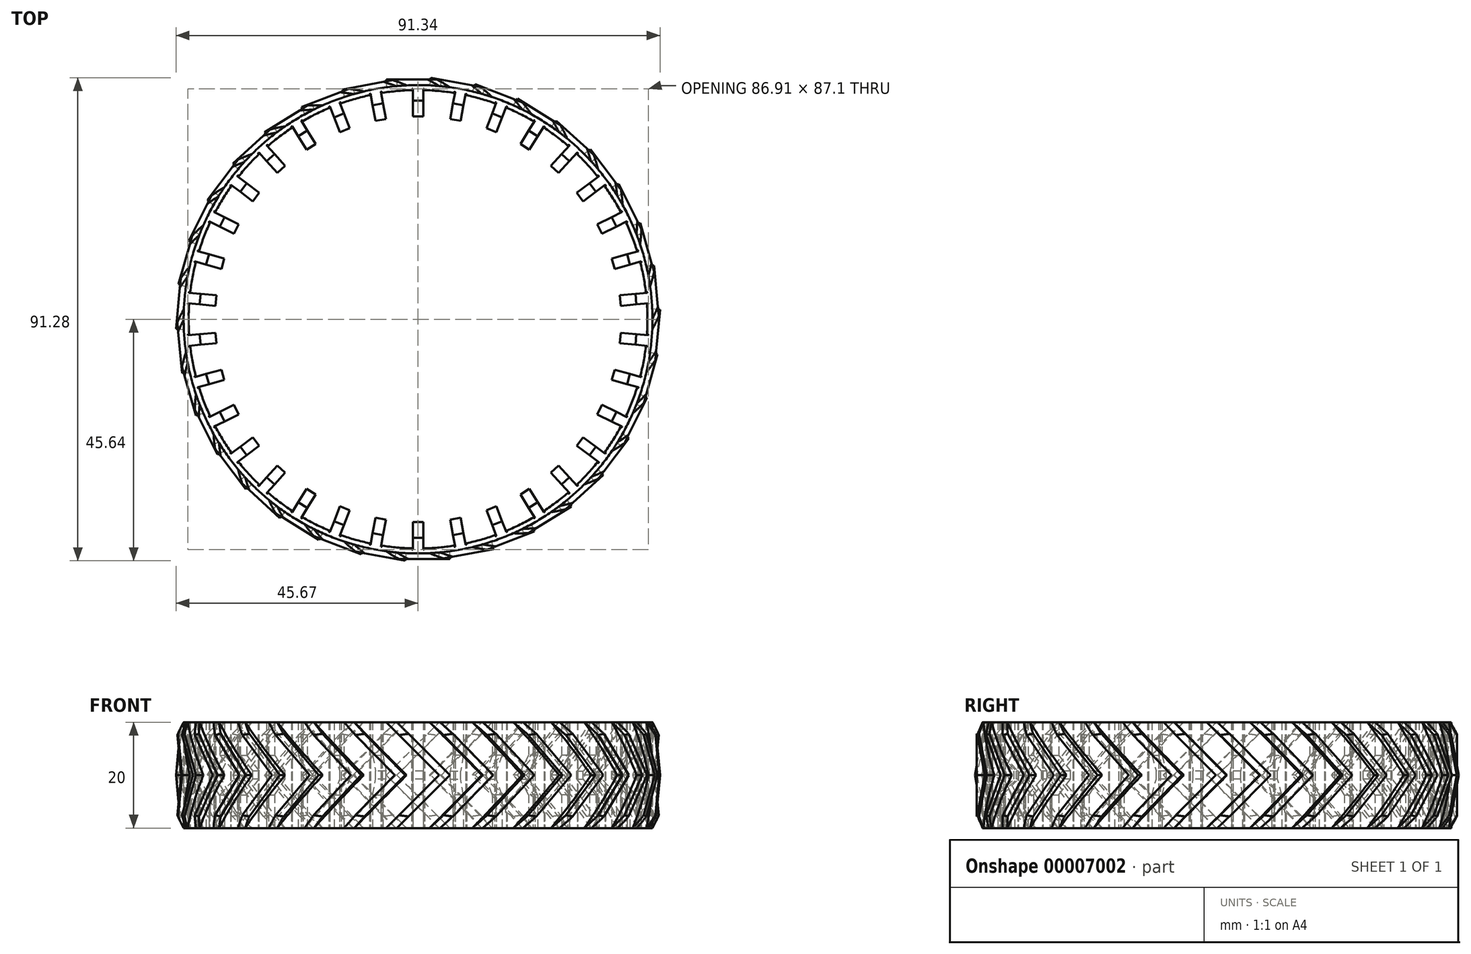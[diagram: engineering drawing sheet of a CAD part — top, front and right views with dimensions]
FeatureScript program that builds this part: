
annotation { "Feature Type Name" : "Feature", "Feature Type Description" : "" }
export const myFeature = defineFeature(function(context is Context, id is Id, definition is map)
    precondition{}
    {
        {
            var Q0;
            Q0=qCreatedBy(makeId("Front.planeOp"),FACE);
            cPlane(context, id + "F0", {"entities" : qUnion([Q0]), "cplaneType" : CPlaneType.OFFSET, "offset" : 86.62 * mm / 2, "width" : 150 * mm, "height" : 150 * mm});
        }
        {
            var Q0;
            Q0=qCreatedBy(id+"F0.planeOp",FACE);
            var sketch = newSketch(context, id + "F1", { "sketchPlane" : qUnion([Q0])});
            skLineSegment(sketch, "E0", {"start": v(-5, -10) * mm, "end": v(-6, -10) * mm});
            skLineSegment(sketch, "E1", {"start": v(-5, -10) * mm, "end": v(-4, -10) * mm});
            skLineSegment(sketch, "E2", {"start": v(-5, 10) * mm, "end": v(-4, 10) * mm});
            skLineSegment(sketch, "E3", {"start": v(-5, 10) * mm, "end": v(-6, 10) * mm});
            skLineSegment(sketch, "E4", {"start": v(-6, 10) * mm, "end": v(4, 0) * mm});
            skLineSegment(sketch, "E5", {"start": v(4, 0) * mm, "end": v(-6, -10) * mm});
            skLineSegment(sketch, "E6", {"start": v(-4, -10) * mm, "end": v(6, 0) * mm});
            skLineSegment(sketch, "E7", {"start": v(6, 0) * mm, "end": v(-4, 10) * mm});
            skSolve(sketch);
        }
        {
            var Q0;
            Q0 = qSketchRegion(id + "F1", true);
            extrude(context, id + "F2", {"entities" : qUnion([Q0]), "depth" : 2 * mm, "hasSecondDirection" : true, "secondDirectionOppositeDirection" : true, "secondDirectionDepth" : 2 * mm});
        }
        {
            var Q0;
            Q0=qCreatedBy(makeId("Front.planeOp"),FACE);
            var sketch = newSketch(context, id + "F3", { "sketchPlane" : qUnion([Q0])});
            skLineSegment(sketch, "E8", {"start": v(0, 0) * mm, "end": v(0, 18.84) * mm, "construction": true});
            skSolve(sketch);
        }
        {
            var Q0;
            Q0=makeQuery(id+"F2.opExtrude","SWEPT_BODY",BODY,{"disambiguationData":[OSD([sQuery(id+"F1.wireOp",EDGE,"E0"),sQuery(id+"F1.wireOp",EDGE,"E1"),sQuery(id+"F1.wireOp",EDGE,"E2"),sQuery(id+"F1.wireOp",EDGE,"E3"),sQuery(id+"F1.wireOp",EDGE,"E4"),sQuery(id+"F1.wireOp",EDGE,"E5"),sQuery(id+"F1.wireOp",EDGE,"E6"),sQuery(id+"F1.wireOp",EDGE,"E7")])]});
            var Q1;
            Q1=sQuery(id+"F3.wireOp",EDGE,"E8");
            circularPattern(context, id + "F4", {"operationType" : NewBodyOperationType.ADD, "entities" : qUnion([Q0]), "axis" : qUnion([Q1]), "angle" : 360 * degree, "instanceCount" : 34, "equalSpace" : true});
        }
        {
            var Q0;
            Q0=qCreatedBy(makeId("Top.planeOp"),FACE);
            var sketch = newSketch(context, id + "F5", { "sketchPlane" : qUnion([Q0])});
            skCircle(sketch, "E9", {"center": v(0, 0) * mm, "radius": 43.31 * mm});
            skSolve(sketch);
        }
        {
            var Q0;
            Q0 = qSketchRegion(id + "F5", true);
            extrude(context, id + "F6", {"entities" : qUnion([Q0]), "operationType" : NewBodyOperationType.REMOVE, "oppositeDirection" : true, "depth" : 25 * mm, "hasSecondDirection" : true, "secondDirectionOppositeDirection" : false, "secondDirectionDepth" : 25 * mm});
        }
        {
            var Q0;
            Q0=qCreatedBy(makeId("Top.planeOp"),FACE);
            var sketch = newSketch(context, id + "F7", { "sketchPlane" : qUnion([Q0])});
            skLineSegment(sketch, "E10", {"start": v(0, 41.31) * mm, "end": v(1, 41.31) * mm});
            skLineSegment(sketch, "E11", {"start": v(0, 41.31) * mm, "end": v(-1, 41.31) * mm});
            skLineSegment(sketch, "E12", {"start": v(1, 41.31) * mm, "end": v(1, 43.3) * mm});
            skLineSegment(sketch, "E13", {"start": v(-1, 41.31) * mm, "end": v(-1, 43.3) * mm});
            skArc(sketch, "E14", {"start": v(1.25, 43.3) * mm, "mid": v(1.18, 43.47) * mm, "end": v(1, 43.55) * mm});
            skLineSegment(sketch, "E15", {"start": v(-1, 43.3) * mm, "end": v(-1, 43.55) * mm});
            skLineSegment(sketch, "E16", {"start": v(1, 43.3) * mm, "end": v(1, 43.55) * mm});
            skLineSegment(sketch, "E17", {"start": v(1.25, 43.3) * mm, "end": v(1.25, 43.3) * mm});
            skLineSegment(sketch, "E18", {"start": v(-1.25, 43.3) * mm, "end": v(-1.25, 43.3) * mm});
            skArc(sketch, "E19.trimOffspring", {"start": v(-1, 43.55) * mm, "mid": v(-1.18, 43.47) * mm, "end": v(-1.25, 43.3) * mm});
            skArc(sketch, "E20.trimOffspring", {"start": v(6.73, 42.78) * mm, "mid": v(4, 43.13) * mm, "end": v(1.25, 43.3) * mm});
            skArc(sketch, "E21.1.0", {"start": v(-1.25, 43.3) * mm, "mid": v(-4, 43.13) * mm, "end": v(-6.73, 42.78) * mm});
            skLineSegment(sketch, "E21.1.1", {"start": v(-6.6, 40.8) * mm, "end": v(-6.97, 42.74) * mm});
            skLineSegment(sketch, "E21.1.2", {"start": v(-8.57, 40.42) * mm, "end": v(-8.94, 42.38) * mm});
            skLineSegment(sketch, "E21.1.3", {"start": v(-7.6, 40.6) * mm, "end": v(-6.6, 40.8) * mm});
            skLineSegment(sketch, "E21.1.4", {"start": v(-7.6, 40.6) * mm, "end": v(-8.57, 40.42) * mm});
            skLineSegment(sketch, "E21.1.5", {"start": v(-8.94, 42.38) * mm, "end": v(-8.98, 42.62) * mm});
            skArc(sketch, "E21.1.6", {"start": v(-8.98, 42.62) * mm, "mid": v(-9.15, 42.52) * mm, "end": v(-9.18, 42.33) * mm});
            skArc(sketch, "E21.1.7", {"start": v(-6.73, 42.78) * mm, "mid": v(-6.83, 42.95) * mm, "end": v(-7.02, 43) * mm});
            skLineSegment(sketch, "E21.1.8", {"start": v(-6.97, 42.74) * mm, "end": v(-7.02, 43) * mm});
            skLineSegment(sketch, "E21.1.9", {"start": v(-6.73, 42.79) * mm, "end": v(-6.73, 42.78) * mm});
            skLineSegment(sketch, "E21.1.10", {"start": v(-9.18, 42.33) * mm, "end": v(-9.18, 42.33) * mm});
            skArc(sketch, "E21.2.0", {"start": v(-9.18, 42.33) * mm, "mid": v(-11.85, 41.66) * mm, "end": v(-14.47, 40.82) * mm});
            skLineSegment(sketch, "E21.2.1", {"start": v(-14, 38.88) * mm, "end": v(-14.7, 40.74) * mm});
            skLineSegment(sketch, "E21.2.2", {"start": v(-15.86, 38.16) * mm, "end": v(-16.57, 40.01) * mm});
            skLineSegment(sketch, "E21.2.3", {"start": v(-14.92, 38.52) * mm, "end": v(-14, 38.88) * mm});
            skLineSegment(sketch, "E21.2.4", {"start": v(-14.92, 38.52) * mm, "end": v(-15.86, 38.16) * mm});
            skLineSegment(sketch, "E21.2.5", {"start": v(-16.57, 40.01) * mm, "end": v(-16.66, 40.25) * mm});
            skArc(sketch, "E21.2.6", {"start": v(-16.66, 40.25) * mm, "mid": v(-16.8, 40.11) * mm, "end": v(-16.8, 39.92) * mm});
            skArc(sketch, "E21.2.7", {"start": v(-14.47, 40.82) * mm, "mid": v(-14.6, 40.96) * mm, "end": v(-14.8, 40.97) * mm});
            skLineSegment(sketch, "E21.2.8", {"start": v(-14.7, 40.74) * mm, "end": v(-14.8, 40.97) * mm});
            skLineSegment(sketch, "E21.2.9", {"start": v(-14.47, 40.82) * mm, "end": v(-14.47, 40.82) * mm});
            skLineSegment(sketch, "E21.2.10", {"start": v(-16.8, 39.92) * mm, "end": v(-16.8, 39.92) * mm});
            skArc(sketch, "E21.3.0", {"start": v(-16.8, 39.92) * mm, "mid": v(-19.3, 38.77) * mm, "end": v(-21.73, 37.47) * mm});
            skLineSegment(sketch, "E21.3.1", {"start": v(-20.9, 35.65) * mm, "end": v(-21.94, 37.34) * mm});
            skLineSegment(sketch, "E21.3.2", {"start": v(-22.6, 34.6) * mm, "end": v(-23.64, 36.29) * mm});
            skLineSegment(sketch, "E21.3.3", {"start": v(-21.75, 35.12) * mm, "end": v(-20.9, 35.65) * mm});
            skLineSegment(sketch, "E21.3.4", {"start": v(-21.75, 35.12) * mm, "end": v(-22.6, 34.6) * mm});
            skLineSegment(sketch, "E21.3.5", {"start": v(-23.64, 36.29) * mm, "end": v(-23.78, 36.5) * mm});
            skArc(sketch, "E21.3.6", {"start": v(-23.78, 36.5) * mm, "mid": v(-23.89, 36.34) * mm, "end": v(-23.85, 36.15) * mm});
            skArc(sketch, "E21.3.7", {"start": v(-21.73, 37.47) * mm, "mid": v(-21.88, 37.58) * mm, "end": v(-22.08, 37.55) * mm});
            skLineSegment(sketch, "E21.3.8", {"start": v(-21.94, 37.34) * mm, "end": v(-22.08, 37.55) * mm});
            skLineSegment(sketch, "E21.3.9", {"start": v(-21.73, 37.47) * mm, "end": v(-21.73, 37.47) * mm});
            skLineSegment(sketch, "E21.3.10", {"start": v(-23.86, 36.16) * mm, "end": v(-23.85, 36.15) * mm});
            skArc(sketch, "E21.4.0", {"start": v(-23.85, 36.15) * mm, "mid": v(-26.1, 34.56) * mm, "end": v(-28.24, 32.84) * mm});
            skLineSegment(sketch, "E21.4.1", {"start": v(-27.1, 31.2) * mm, "end": v(-28.43, 32.67) * mm});
            skLineSegment(sketch, "E21.4.2", {"start": v(-28.57, 29.85) * mm, "end": v(-29.9, 31.32) * mm});
            skLineSegment(sketch, "E21.4.3", {"start": v(-27.83, 30.53) * mm, "end": v(-27.1, 31.2) * mm});
            skLineSegment(sketch, "E21.4.4", {"start": v(-27.83, 30.53) * mm, "end": v(-28.57, 29.85) * mm});
            skLineSegment(sketch, "E21.4.5", {"start": v(-29.9, 31.32) * mm, "end": v(-30.08, 31.5) * mm});
            skArc(sketch, "E21.4.6", {"start": v(-30.08, 31.5) * mm, "mid": v(-30.16, 31.33) * mm, "end": v(-30.09, 31.15) * mm});
            skArc(sketch, "E21.4.7", {"start": v(-28.24, 32.84) * mm, "mid": v(-28.42, 32.92) * mm, "end": v(-28.6, 32.86) * mm});
            skLineSegment(sketch, "E21.4.8", {"start": v(-28.43, 32.67) * mm, "end": v(-28.6, 32.86) * mm});
            skLineSegment(sketch, "E21.4.9", {"start": v(-28.24, 32.84) * mm, "end": v(-28.24, 32.84) * mm});
            skLineSegment(sketch, "E21.4.10", {"start": v(-30.1, 31.16) * mm, "end": v(-30.09, 31.15) * mm});
            skArc(sketch, "E21.5.0", {"start": v(-30.09, 31.15) * mm, "mid": v(-32, 29.18) * mm, "end": v(-33.8, 27.09) * mm});
            skLineSegment(sketch, "E21.5.1", {"start": v(-32.36, 25.7) * mm, "end": v(-33.95, 26.9) * mm});
            skLineSegment(sketch, "E21.5.2", {"start": v(-33.57, 24.1) * mm, "end": v(-35.16, 25.3) * mm});
            skLineSegment(sketch, "E21.5.3", {"start": v(-32.97, 24.9) * mm, "end": v(-32.36, 25.7) * mm});
            skLineSegment(sketch, "E21.5.4", {"start": v(-32.97, 24.9) * mm, "end": v(-33.57, 24.1) * mm});
            skLineSegment(sketch, "E21.5.5", {"start": v(-35.16, 25.3) * mm, "end": v(-35.36, 25.45) * mm});
            skArc(sketch, "E21.5.6", {"start": v(-35.36, 25.45) * mm, "mid": v(-35.4, 25.26) * mm, "end": v(-35.3, 25.1) * mm});
            skArc(sketch, "E21.5.7", {"start": v(-33.8, 27.09) * mm, "mid": v(-33.98, 27.14) * mm, "end": v(-34.15, 27.04) * mm});
            skLineSegment(sketch, "E21.5.8", {"start": v(-33.95, 26.9) * mm, "end": v(-34.15, 27.04) * mm});
            skLineSegment(sketch, "E21.5.9", {"start": v(-33.8, 27.09) * mm, "end": v(-33.8, 27.09) * mm});
            skLineSegment(sketch, "E21.5.10", {"start": v(-35.3, 25.1) * mm, "end": v(-35.3, 25.1) * mm});
            skArc(sketch, "E21.6.0", {"start": v(-35.3, 25.1) * mm, "mid": v(-36.82, 22.8) * mm, "end": v(-38.2, 20.42) * mm});
            skLineSegment(sketch, "E21.6.1", {"start": v(-36.53, 19.3) * mm, "end": v(-38.31, 20.2) * mm});
            skLineSegment(sketch, "E21.6.2", {"start": v(-37.42, 17.52) * mm, "end": v(-39.2, 18.4) * mm});
            skLineSegment(sketch, "E21.6.3", {"start": v(-36.98, 18.41) * mm, "end": v(-36.53, 19.3) * mm});
            skLineSegment(sketch, "E21.6.4", {"start": v(-36.98, 18.41) * mm, "end": v(-37.42, 17.52) * mm});
            skLineSegment(sketch, "E21.6.5", {"start": v(-39.2, 18.4) * mm, "end": v(-39.43, 18.52) * mm});
            skArc(sketch, "E21.6.6", {"start": v(-39.43, 18.52) * mm, "mid": v(-39.44, 18.32) * mm, "end": v(-39.31, 18.18) * mm});
            skArc(sketch, "E21.6.7", {"start": v(-38.2, 20.42) * mm, "mid": v(-38.39, 20.43) * mm, "end": v(-38.54, 20.3) * mm});
            skLineSegment(sketch, "E21.6.8", {"start": v(-38.31, 20.2) * mm, "end": v(-38.54, 20.3) * mm});
            skLineSegment(sketch, "E21.6.9", {"start": v(-38.2, 20.42) * mm, "end": v(-38.2, 20.42) * mm});
            skLineSegment(sketch, "E21.6.10", {"start": v(-39.32, 18.18) * mm, "end": v(-39.31, 18.18) * mm});
            skArc(sketch, "E21.7.0", {"start": v(-39.31, 18.18) * mm, "mid": v(-40.39, 15.65) * mm, "end": v(-41.3, 13.05) * mm});
            skLineSegment(sketch, "E21.7.1", {"start": v(-39.46, 12.27) * mm, "end": v(-41.37, 12.81) * mm});
            skLineSegment(sketch, "E21.7.2", {"start": v(-40, 10.34) * mm, "end": v(-41.92, 10.89) * mm});
            skLineSegment(sketch, "E21.7.3", {"start": v(-39.73, 11.3) * mm, "end": v(-39.46, 12.27) * mm});
            skLineSegment(sketch, "E21.7.4", {"start": v(-39.73, 11.3) * mm, "end": v(-40, 10.34) * mm});
            skLineSegment(sketch, "E21.7.5", {"start": v(-41.92, 10.89) * mm, "end": v(-42.16, 10.96) * mm});
            skArc(sketch, "E21.7.6", {"start": v(-42.16, 10.96) * mm, "mid": v(-42.14, 10.76) * mm, "end": v(-41.98, 10.65) * mm});
            skArc(sketch, "E21.7.7", {"start": v(-41.3, 13.05) * mm, "mid": v(-41.5, 13.03) * mm, "end": v(-41.61, 12.88) * mm});
            skLineSegment(sketch, "E21.7.8", {"start": v(-41.37, 12.81) * mm, "end": v(-41.61, 12.88) * mm});
            skLineSegment(sketch, "E21.7.9", {"start": v(-41.3, 13.05) * mm, "end": v(-41.3, 13.05) * mm});
            skLineSegment(sketch, "E21.7.10", {"start": v(-41.99, 10.65) * mm, "end": v(-41.98, 10.65) * mm});
            skArc(sketch, "E21.8.0", {"start": v(-41.98, 10.65) * mm, "mid": v(-42.57, 7.96) * mm, "end": v(-43, 5.24) * mm});
            skLineSegment(sketch, "E21.8.1", {"start": v(-41.04, 4.8) * mm, "end": v(-43.02, 5) * mm});
            skLineSegment(sketch, "E21.8.2", {"start": v(-41.23, 2.82) * mm, "end": v(-43.2, 3) * mm});
            skLineSegment(sketch, "E21.8.3", {"start": v(-41.13, 3.81) * mm, "end": v(-41.04, 4.8) * mm});
            skLineSegment(sketch, "E21.8.4", {"start": v(-41.13, 3.81) * mm, "end": v(-41.23, 2.82) * mm});
            skLineSegment(sketch, "E21.8.5", {"start": v(-43.2, 3) * mm, "end": v(-43.45, 3.02) * mm});
            skArc(sketch, "E21.8.6", {"start": v(-43.45, 3.02) * mm, "mid": v(-43.4, 2.84) * mm, "end": v(-43.22, 2.75) * mm});
            skArc(sketch, "E21.8.7", {"start": v(-43, 5.24) * mm, "mid": v(-43.18, 5.19) * mm, "end": v(-43.27, 5.01) * mm});
            skLineSegment(sketch, "E21.8.8", {"start": v(-43.02, 5) * mm, "end": v(-43.27, 5.01) * mm});
            skLineSegment(sketch, "E21.8.9", {"start": v(-43, 5.24) * mm, "end": v(-43, 5.24) * mm});
            skLineSegment(sketch, "E21.8.10", {"start": v(-43.23, 2.75) * mm, "end": v(-43.22, 2.75) * mm});
            skArc(sketch, "E21.9.0", {"start": v(-43.22, 2.75) * mm, "mid": v(-43.31, 0) * mm, "end": v(-43.22, -2.75) * mm});
            skLineSegment(sketch, "E21.9.1", {"start": v(-41.23, -2.82) * mm, "end": v(-43.2, -3) * mm});
            skLineSegment(sketch, "E21.9.2", {"start": v(-41.04, -4.8) * mm, "end": v(-43.02, -5) * mm});
            skLineSegment(sketch, "E21.9.3", {"start": v(-41.13, -3.81) * mm, "end": v(-41.23, -2.82) * mm});
            skLineSegment(sketch, "E21.9.4", {"start": v(-41.13, -3.81) * mm, "end": v(-41.04, -4.8) * mm});
            skLineSegment(sketch, "E21.9.5", {"start": v(-43.02, -5) * mm, "end": v(-43.27, -5.01) * mm});
            skArc(sketch, "E21.9.6", {"start": v(-43.27, -5.01) * mm, "mid": v(-43.18, -5.19) * mm, "end": v(-43, -5.24) * mm});
            skArc(sketch, "E21.9.7", {"start": v(-43.22, -2.75) * mm, "mid": v(-43.4, -2.84) * mm, "end": v(-43.45, -3.02) * mm});
            skLineSegment(sketch, "E21.9.8", {"start": v(-43.2, -3) * mm, "end": v(-43.45, -3.02) * mm});
            skLineSegment(sketch, "E21.9.9", {"start": v(-43.22, -2.75) * mm, "end": v(-43.22, -2.75) * mm});
            skLineSegment(sketch, "E21.9.10", {"start": v(-43, -5.24) * mm, "end": v(-43, -5.24) * mm});
            skArc(sketch, "E21.10.0", {"start": v(-43, -5.24) * mm, "mid": v(-42.57, -7.96) * mm, "end": v(-41.98, -10.65) * mm});
            skLineSegment(sketch, "E21.10.1", {"start": v(-40, -10.34) * mm, "end": v(-41.92, -10.89) * mm});
            skLineSegment(sketch, "E21.10.2", {"start": v(-39.46, -12.27) * mm, "end": v(-41.37, -12.81) * mm});
            skLineSegment(sketch, "E21.10.3", {"start": v(-39.73, -11.3) * mm, "end": v(-40, -10.34) * mm});
            skLineSegment(sketch, "E21.10.4", {"start": v(-39.73, -11.3) * mm, "end": v(-39.46, -12.27) * mm});
            skLineSegment(sketch, "E21.10.5", {"start": v(-41.37, -12.81) * mm, "end": v(-41.61, -12.88) * mm});
            skArc(sketch, "E21.10.6", {"start": v(-41.61, -12.88) * mm, "mid": v(-41.5, -13.03) * mm, "end": v(-41.3, -13.05) * mm});
            skArc(sketch, "E21.10.7", {"start": v(-41.98, -10.65) * mm, "mid": v(-42.14, -10.76) * mm, "end": v(-42.16, -10.96) * mm});
            skLineSegment(sketch, "E21.10.8", {"start": v(-41.92, -10.89) * mm, "end": v(-42.16, -10.96) * mm});
            skLineSegment(sketch, "E21.10.9", {"start": v(-41.98, -10.65) * mm, "end": v(-41.98, -10.65) * mm});
            skLineSegment(sketch, "E21.10.10", {"start": v(-41.3, -13.05) * mm, "end": v(-41.3, -13.05) * mm});
            skArc(sketch, "E21.11.0", {"start": v(-41.3, -13.05) * mm, "mid": v(-40.39, -15.65) * mm, "end": v(-39.31, -18.18) * mm});
            skLineSegment(sketch, "E21.11.1", {"start": v(-37.42, -17.52) * mm, "end": v(-39.2, -18.4) * mm});
            skLineSegment(sketch, "E21.11.2", {"start": v(-36.53, -19.3) * mm, "end": v(-38.31, -20.2) * mm});
            skLineSegment(sketch, "E21.11.3", {"start": v(-36.98, -18.41) * mm, "end": v(-37.42, -17.52) * mm});
            skLineSegment(sketch, "E21.11.4", {"start": v(-36.98, -18.41) * mm, "end": v(-36.53, -19.3) * mm});
            skLineSegment(sketch, "E21.11.5", {"start": v(-38.31, -20.2) * mm, "end": v(-38.54, -20.3) * mm});
            skArc(sketch, "E21.11.6", {"start": v(-38.54, -20.3) * mm, "mid": v(-38.39, -20.43) * mm, "end": v(-38.2, -20.42) * mm});
            skArc(sketch, "E21.11.7", {"start": v(-39.31, -18.18) * mm, "mid": v(-39.44, -18.32) * mm, "end": v(-39.43, -18.52) * mm});
            skLineSegment(sketch, "E21.11.8", {"start": v(-39.2, -18.4) * mm, "end": v(-39.43, -18.52) * mm});
            skLineSegment(sketch, "E21.11.9", {"start": v(-39.31, -18.18) * mm, "end": v(-39.31, -18.18) * mm});
            skLineSegment(sketch, "E21.11.10", {"start": v(-38.2, -20.42) * mm, "end": v(-38.2, -20.42) * mm});
            skArc(sketch, "E21.12.0", {"start": v(-38.2, -20.42) * mm, "mid": v(-36.82, -22.8) * mm, "end": v(-35.3, -25.1) * mm});
            skLineSegment(sketch, "E21.12.1", {"start": v(-33.57, -24.1) * mm, "end": v(-35.16, -25.3) * mm});
            skLineSegment(sketch, "E21.12.2", {"start": v(-32.36, -25.7) * mm, "end": v(-33.95, -26.9) * mm});
            skLineSegment(sketch, "E21.12.3", {"start": v(-32.97, -24.9) * mm, "end": v(-33.57, -24.1) * mm});
            skLineSegment(sketch, "E21.12.4", {"start": v(-32.97, -24.9) * mm, "end": v(-32.36, -25.7) * mm});
            skLineSegment(sketch, "E21.12.5", {"start": v(-33.95, -26.9) * mm, "end": v(-34.15, -27.04) * mm});
            skArc(sketch, "E21.12.6", {"start": v(-34.15, -27.04) * mm, "mid": v(-33.98, -27.14) * mm, "end": v(-33.8, -27.09) * mm});
            skArc(sketch, "E21.12.7", {"start": v(-35.3, -25.1) * mm, "mid": v(-35.4, -25.26) * mm, "end": v(-35.36, -25.45) * mm});
            skLineSegment(sketch, "E21.12.8", {"start": v(-35.16, -25.3) * mm, "end": v(-35.36, -25.45) * mm});
            skLineSegment(sketch, "E21.12.9", {"start": v(-35.3, -25.1) * mm, "end": v(-35.3, -25.1) * mm});
            skLineSegment(sketch, "E21.12.10", {"start": v(-33.8, -27.1) * mm, "end": v(-33.8, -27.09) * mm});
            skArc(sketch, "E21.13.0", {"start": v(-33.8, -27.09) * mm, "mid": v(-32, -29.18) * mm, "end": v(-30.09, -31.15) * mm});
            skLineSegment(sketch, "E21.13.1", {"start": v(-28.57, -29.85) * mm, "end": v(-29.9, -31.32) * mm});
            skLineSegment(sketch, "E21.13.2", {"start": v(-27.1, -31.2) * mm, "end": v(-28.43, -32.67) * mm});
            skLineSegment(sketch, "E21.13.3", {"start": v(-27.83, -30.53) * mm, "end": v(-28.57, -29.85) * mm});
            skLineSegment(sketch, "E21.13.4", {"start": v(-27.83, -30.53) * mm, "end": v(-27.1, -31.2) * mm});
            skLineSegment(sketch, "E21.13.5", {"start": v(-28.43, -32.67) * mm, "end": v(-28.6, -32.86) * mm});
            skArc(sketch, "E21.13.6", {"start": v(-28.6, -32.86) * mm, "mid": v(-28.42, -32.92) * mm, "end": v(-28.24, -32.84) * mm});
            skArc(sketch, "E21.13.7", {"start": v(-30.09, -31.15) * mm, "mid": v(-30.16, -31.33) * mm, "end": v(-30.08, -31.5) * mm});
            skLineSegment(sketch, "E21.13.8", {"start": v(-29.9, -31.32) * mm, "end": v(-30.08, -31.5) * mm});
            skLineSegment(sketch, "E21.13.9", {"start": v(-30.09, -31.15) * mm, "end": v(-30.09, -31.15) * mm});
            skLineSegment(sketch, "E21.13.10", {"start": v(-28.25, -32.84) * mm, "end": v(-28.24, -32.84) * mm});
            skArc(sketch, "E21.14.0", {"start": v(-28.24, -32.84) * mm, "mid": v(-26.1, -34.56) * mm, "end": v(-23.85, -36.15) * mm});
            skLineSegment(sketch, "E21.14.1", {"start": v(-22.6, -34.6) * mm, "end": v(-23.64, -36.29) * mm});
            skLineSegment(sketch, "E21.14.2", {"start": v(-20.9, -35.65) * mm, "end": v(-21.94, -37.34) * mm});
            skLineSegment(sketch, "E21.14.3", {"start": v(-21.75, -35.12) * mm, "end": v(-22.6, -34.6) * mm});
            skLineSegment(sketch, "E21.14.4", {"start": v(-21.75, -35.12) * mm, "end": v(-20.9, -35.65) * mm});
            skLineSegment(sketch, "E21.14.5", {"start": v(-21.94, -37.34) * mm, "end": v(-22.08, -37.55) * mm});
            skArc(sketch, "E21.14.6", {"start": v(-22.08, -37.55) * mm, "mid": v(-21.88, -37.58) * mm, "end": v(-21.73, -37.47) * mm});
            skArc(sketch, "E21.14.7", {"start": v(-23.85, -36.15) * mm, "mid": v(-23.89, -36.34) * mm, "end": v(-23.78, -36.5) * mm});
            skLineSegment(sketch, "E21.14.8", {"start": v(-23.64, -36.29) * mm, "end": v(-23.78, -36.5) * mm});
            skLineSegment(sketch, "E21.14.9", {"start": v(-23.85, -36.15) * mm, "end": v(-23.85, -36.15) * mm});
            skLineSegment(sketch, "E21.14.10", {"start": v(-21.73, -37.47) * mm, "end": v(-21.73, -37.47) * mm});
            skArc(sketch, "E21.15.0", {"start": v(-21.73, -37.47) * mm, "mid": v(-19.3, -38.77) * mm, "end": v(-16.8, -39.92) * mm});
            skLineSegment(sketch, "E21.15.1", {"start": v(-15.86, -38.16) * mm, "end": v(-16.57, -40.01) * mm});
            skLineSegment(sketch, "E21.15.2", {"start": v(-14, -38.88) * mm, "end": v(-14.7, -40.74) * mm});
            skLineSegment(sketch, "E21.15.3", {"start": v(-14.92, -38.52) * mm, "end": v(-15.86, -38.16) * mm});
            skLineSegment(sketch, "E21.15.4", {"start": v(-14.92, -38.52) * mm, "end": v(-14, -38.88) * mm});
            skLineSegment(sketch, "E21.15.5", {"start": v(-14.7, -40.74) * mm, "end": v(-14.8, -40.97) * mm});
            skArc(sketch, "E21.15.6", {"start": v(-14.8, -40.97) * mm, "mid": v(-14.6, -40.96) * mm, "end": v(-14.47, -40.82) * mm});
            skArc(sketch, "E21.15.7", {"start": v(-16.8, -39.92) * mm, "mid": v(-16.8, -40.11) * mm, "end": v(-16.66, -40.25) * mm});
            skLineSegment(sketch, "E21.15.8", {"start": v(-16.57, -40.01) * mm, "end": v(-16.66, -40.25) * mm});
            skLineSegment(sketch, "E21.15.9", {"start": v(-16.8, -39.92) * mm, "end": v(-16.8, -39.92) * mm});
            skLineSegment(sketch, "E21.15.10", {"start": v(-14.48, -40.83) * mm, "end": v(-14.47, -40.82) * mm});
            skArc(sketch, "E21.16.0", {"start": v(-14.47, -40.82) * mm, "mid": v(-11.85, -41.66) * mm, "end": v(-9.18, -42.33) * mm});
            skLineSegment(sketch, "E21.16.1", {"start": v(-8.57, -40.42) * mm, "end": v(-8.94, -42.38) * mm});
            skLineSegment(sketch, "E21.16.2", {"start": v(-6.6, -40.8) * mm, "end": v(-6.97, -42.74) * mm});
            skLineSegment(sketch, "E21.16.3", {"start": v(-7.6, -40.6) * mm, "end": v(-8.57, -40.42) * mm});
            skLineSegment(sketch, "E21.16.4", {"start": v(-7.6, -40.6) * mm, "end": v(-6.6, -40.8) * mm});
            skLineSegment(sketch, "E21.16.5", {"start": v(-6.97, -42.74) * mm, "end": v(-7.02, -43) * mm});
            skArc(sketch, "E21.16.6", {"start": v(-7.02, -43) * mm, "mid": v(-6.83, -42.95) * mm, "end": v(-6.73, -42.78) * mm});
            skArc(sketch, "E21.16.7", {"start": v(-9.18, -42.33) * mm, "mid": v(-9.15, -42.52) * mm, "end": v(-8.98, -42.62) * mm});
            skLineSegment(sketch, "E21.16.8", {"start": v(-8.94, -42.38) * mm, "end": v(-8.98, -42.62) * mm});
            skLineSegment(sketch, "E21.16.9", {"start": v(-9.18, -42.33) * mm, "end": v(-9.18, -42.33) * mm});
            skLineSegment(sketch, "E21.16.10", {"start": v(-6.73, -42.8) * mm, "end": v(-6.73, -42.78) * mm});
            skArc(sketch, "E21.17.0", {"start": v(-6.73, -42.78) * mm, "mid": v(-4, -43.13) * mm, "end": v(-1.25, -43.3) * mm});
            skLineSegment(sketch, "E21.17.1", {"start": v(-1, -41.31) * mm, "end": v(-1, -43.3) * mm});
            skLineSegment(sketch, "E21.17.2", {"start": v(1, -41.31) * mm, "end": v(1, -43.3) * mm});
            skLineSegment(sketch, "E21.17.3", {"start": v(0, -41.31) * mm, "end": v(-1, -41.31) * mm});
            skLineSegment(sketch, "E21.17.4", {"start": v(0, -41.31) * mm, "end": v(1, -41.31) * mm});
            skLineSegment(sketch, "E21.17.5", {"start": v(1, -43.3) * mm, "end": v(1, -43.55) * mm});
            skArc(sketch, "E21.17.6", {"start": v(1, -43.55) * mm, "mid": v(1.18, -43.47) * mm, "end": v(1.25, -43.3) * mm});
            skArc(sketch, "E21.17.7", {"start": v(-1.25, -43.3) * mm, "mid": v(-1.18, -43.47) * mm, "end": v(-1, -43.55) * mm});
            skLineSegment(sketch, "E21.17.8", {"start": v(-1, -43.3) * mm, "end": v(-1, -43.55) * mm});
            skLineSegment(sketch, "E21.17.9", {"start": v(-1.25, -43.3) * mm, "end": v(-1.25, -43.3) * mm});
            skLineSegment(sketch, "E21.17.10", {"start": v(1.25, -43.3) * mm, "end": v(1.25, -43.3) * mm});
            skArc(sketch, "E21.18.0", {"start": v(1.25, -43.3) * mm, "mid": v(4, -43.13) * mm, "end": v(6.73, -42.78) * mm});
            skLineSegment(sketch, "E21.18.1", {"start": v(6.6, -40.8) * mm, "end": v(6.97, -42.74) * mm});
            skLineSegment(sketch, "E21.18.2", {"start": v(8.57, -40.42) * mm, "end": v(8.94, -42.38) * mm});
            skLineSegment(sketch, "E21.18.3", {"start": v(7.6, -40.6) * mm, "end": v(6.6, -40.8) * mm});
            skLineSegment(sketch, "E21.18.4", {"start": v(7.6, -40.6) * mm, "end": v(8.57, -40.42) * mm});
            skLineSegment(sketch, "E21.18.5", {"start": v(8.94, -42.38) * mm, "end": v(8.98, -42.62) * mm});
            skArc(sketch, "E21.18.6", {"start": v(8.98, -42.62) * mm, "mid": v(9.15, -42.52) * mm, "end": v(9.18, -42.33) * mm});
            skArc(sketch, "E21.18.7", {"start": v(6.73, -42.78) * mm, "mid": v(6.83, -42.95) * mm, "end": v(7.02, -43) * mm});
            skLineSegment(sketch, "E21.18.8", {"start": v(6.97, -42.74) * mm, "end": v(7.02, -43) * mm});
            skLineSegment(sketch, "E21.18.9", {"start": v(6.73, -42.79) * mm, "end": v(6.73, -42.78) * mm});
            skLineSegment(sketch, "E21.18.10", {"start": v(9.18, -42.33) * mm, "end": v(9.18, -42.33) * mm});
            skArc(sketch, "E21.19.0", {"start": v(9.18, -42.33) * mm, "mid": v(11.85, -41.66) * mm, "end": v(14.47, -40.82) * mm});
            skLineSegment(sketch, "E21.19.1", {"start": v(14, -38.88) * mm, "end": v(14.7, -40.74) * mm});
            skLineSegment(sketch, "E21.19.2", {"start": v(15.86, -38.16) * mm, "end": v(16.57, -40.01) * mm});
            skLineSegment(sketch, "E21.19.3", {"start": v(14.92, -38.52) * mm, "end": v(14, -38.88) * mm});
            skLineSegment(sketch, "E21.19.4", {"start": v(14.92, -38.52) * mm, "end": v(15.86, -38.16) * mm});
            skLineSegment(sketch, "E21.19.5", {"start": v(16.57, -40.01) * mm, "end": v(16.66, -40.25) * mm});
            skArc(sketch, "E21.19.6", {"start": v(16.66, -40.25) * mm, "mid": v(16.8, -40.11) * mm, "end": v(16.8, -39.92) * mm});
            skArc(sketch, "E21.19.7", {"start": v(14.47, -40.82) * mm, "mid": v(14.6, -40.96) * mm, "end": v(14.8, -40.97) * mm});
            skLineSegment(sketch, "E21.19.8", {"start": v(14.7, -40.74) * mm, "end": v(14.8, -40.97) * mm});
            skLineSegment(sketch, "E21.19.9", {"start": v(14.47, -40.82) * mm, "end": v(14.47, -40.82) * mm});
            skLineSegment(sketch, "E21.19.10", {"start": v(16.8, -39.92) * mm, "end": v(16.8, -39.92) * mm});
            skArc(sketch, "E21.20.0", {"start": v(16.8, -39.92) * mm, "mid": v(19.3, -38.77) * mm, "end": v(21.73, -37.47) * mm});
            skLineSegment(sketch, "E21.20.1", {"start": v(20.9, -35.65) * mm, "end": v(21.94, -37.34) * mm});
            skLineSegment(sketch, "E21.20.2", {"start": v(22.6, -34.6) * mm, "end": v(23.64, -36.29) * mm});
            skLineSegment(sketch, "E21.20.3", {"start": v(21.75, -35.12) * mm, "end": v(20.9, -35.65) * mm});
            skLineSegment(sketch, "E21.20.4", {"start": v(21.75, -35.12) * mm, "end": v(22.6, -34.6) * mm});
            skLineSegment(sketch, "E21.20.5", {"start": v(23.64, -36.29) * mm, "end": v(23.78, -36.5) * mm});
            skArc(sketch, "E21.20.6", {"start": v(23.78, -36.5) * mm, "mid": v(23.89, -36.34) * mm, "end": v(23.85, -36.15) * mm});
            skArc(sketch, "E21.20.7", {"start": v(21.73, -37.47) * mm, "mid": v(21.88, -37.58) * mm, "end": v(22.08, -37.55) * mm});
            skLineSegment(sketch, "E21.20.8", {"start": v(21.94, -37.34) * mm, "end": v(22.08, -37.55) * mm});
            skLineSegment(sketch, "E21.20.9", {"start": v(21.73, -37.47) * mm, "end": v(21.73, -37.47) * mm});
            skLineSegment(sketch, "E21.20.10", {"start": v(23.86, -36.16) * mm, "end": v(23.85, -36.15) * mm});
            skArc(sketch, "E21.21.0", {"start": v(23.85, -36.15) * mm, "mid": v(26.1, -34.56) * mm, "end": v(28.24, -32.84) * mm});
            skLineSegment(sketch, "E21.21.1", {"start": v(27.1, -31.2) * mm, "end": v(28.43, -32.67) * mm});
            skLineSegment(sketch, "E21.21.2", {"start": v(28.57, -29.85) * mm, "end": v(29.9, -31.32) * mm});
            skLineSegment(sketch, "E21.21.3", {"start": v(27.83, -30.53) * mm, "end": v(27.1, -31.2) * mm});
            skLineSegment(sketch, "E21.21.4", {"start": v(27.83, -30.53) * mm, "end": v(28.57, -29.85) * mm});
            skLineSegment(sketch, "E21.21.5", {"start": v(29.9, -31.32) * mm, "end": v(30.08, -31.5) * mm});
            skArc(sketch, "E21.21.6", {"start": v(30.08, -31.5) * mm, "mid": v(30.16, -31.33) * mm, "end": v(30.09, -31.15) * mm});
            skArc(sketch, "E21.21.7", {"start": v(28.24, -32.84) * mm, "mid": v(28.42, -32.92) * mm, "end": v(28.6, -32.86) * mm});
            skLineSegment(sketch, "E21.21.8", {"start": v(28.43, -32.67) * mm, "end": v(28.6, -32.86) * mm});
            skLineSegment(sketch, "E21.21.9", {"start": v(28.24, -32.84) * mm, "end": v(28.24, -32.84) * mm});
            skLineSegment(sketch, "E21.21.10", {"start": v(30.1, -31.16) * mm, "end": v(30.09, -31.15) * mm});
            skArc(sketch, "E21.22.0", {"start": v(30.09, -31.15) * mm, "mid": v(32, -29.18) * mm, "end": v(33.8, -27.09) * mm});
            skLineSegment(sketch, "E21.22.1", {"start": v(32.36, -25.7) * mm, "end": v(33.95, -26.9) * mm});
            skLineSegment(sketch, "E21.22.2", {"start": v(33.57, -24.1) * mm, "end": v(35.16, -25.3) * mm});
            skLineSegment(sketch, "E21.22.3", {"start": v(32.97, -24.9) * mm, "end": v(32.36, -25.7) * mm});
            skLineSegment(sketch, "E21.22.4", {"start": v(32.97, -24.9) * mm, "end": v(33.57, -24.1) * mm});
            skLineSegment(sketch, "E21.22.5", {"start": v(35.16, -25.3) * mm, "end": v(35.36, -25.45) * mm});
            skArc(sketch, "E21.22.6", {"start": v(35.36, -25.45) * mm, "mid": v(35.4, -25.26) * mm, "end": v(35.3, -25.1) * mm});
            skArc(sketch, "E21.22.7", {"start": v(33.8, -27.09) * mm, "mid": v(33.98, -27.14) * mm, "end": v(34.15, -27.04) * mm});
            skLineSegment(sketch, "E21.22.8", {"start": v(33.95, -26.9) * mm, "end": v(34.15, -27.04) * mm});
            skLineSegment(sketch, "E21.22.9", {"start": v(33.8, -27.09) * mm, "end": v(33.8, -27.09) * mm});
            skLineSegment(sketch, "E21.22.10", {"start": v(35.3, -25.1) * mm, "end": v(35.3, -25.1) * mm});
            skArc(sketch, "E21.23.0", {"start": v(35.3, -25.1) * mm, "mid": v(36.82, -22.8) * mm, "end": v(38.2, -20.42) * mm});
            skLineSegment(sketch, "E21.23.1", {"start": v(36.53, -19.3) * mm, "end": v(38.31, -20.2) * mm});
            skLineSegment(sketch, "E21.23.2", {"start": v(37.42, -17.52) * mm, "end": v(39.2, -18.4) * mm});
            skLineSegment(sketch, "E21.23.3", {"start": v(36.98, -18.41) * mm, "end": v(36.53, -19.3) * mm});
            skLineSegment(sketch, "E21.23.4", {"start": v(36.98, -18.41) * mm, "end": v(37.42, -17.52) * mm});
            skLineSegment(sketch, "E21.23.5", {"start": v(39.2, -18.4) * mm, "end": v(39.43, -18.52) * mm});
            skArc(sketch, "E21.23.6", {"start": v(39.43, -18.52) * mm, "mid": v(39.44, -18.32) * mm, "end": v(39.31, -18.18) * mm});
            skArc(sketch, "E21.23.7", {"start": v(38.2, -20.42) * mm, "mid": v(38.39, -20.43) * mm, "end": v(38.54, -20.3) * mm});
            skLineSegment(sketch, "E21.23.8", {"start": v(38.31, -20.2) * mm, "end": v(38.54, -20.3) * mm});
            skLineSegment(sketch, "E21.23.9", {"start": v(38.2, -20.42) * mm, "end": v(38.2, -20.42) * mm});
            skLineSegment(sketch, "E21.23.10", {"start": v(39.32, -18.18) * mm, "end": v(39.31, -18.18) * mm});
            skArc(sketch, "E21.24.0", {"start": v(39.31, -18.18) * mm, "mid": v(40.39, -15.65) * mm, "end": v(41.3, -13.05) * mm});
            skLineSegment(sketch, "E21.24.1", {"start": v(39.46, -12.27) * mm, "end": v(41.37, -12.81) * mm});
            skLineSegment(sketch, "E21.24.2", {"start": v(40, -10.34) * mm, "end": v(41.92, -10.89) * mm});
            skLineSegment(sketch, "E21.24.3", {"start": v(39.73, -11.3) * mm, "end": v(39.46, -12.27) * mm});
            skLineSegment(sketch, "E21.24.4", {"start": v(39.73, -11.3) * mm, "end": v(40, -10.34) * mm});
            skLineSegment(sketch, "E21.24.5", {"start": v(41.92, -10.89) * mm, "end": v(42.16, -10.96) * mm});
            skArc(sketch, "E21.24.6", {"start": v(42.16, -10.96) * mm, "mid": v(42.14, -10.76) * mm, "end": v(41.98, -10.65) * mm});
            skArc(sketch, "E21.24.7", {"start": v(41.3, -13.05) * mm, "mid": v(41.5, -13.03) * mm, "end": v(41.61, -12.88) * mm});
            skLineSegment(sketch, "E21.24.8", {"start": v(41.37, -12.81) * mm, "end": v(41.61, -12.88) * mm});
            skLineSegment(sketch, "E21.24.9", {"start": v(41.3, -13.05) * mm, "end": v(41.3, -13.05) * mm});
            skLineSegment(sketch, "E21.24.10", {"start": v(41.99, -10.65) * mm, "end": v(41.98, -10.65) * mm});
            skArc(sketch, "E21.25.0", {"start": v(41.98, -10.65) * mm, "mid": v(42.57, -7.96) * mm, "end": v(43, -5.24) * mm});
            skLineSegment(sketch, "E21.25.1", {"start": v(41.04, -4.8) * mm, "end": v(43.02, -5) * mm});
            skLineSegment(sketch, "E21.25.2", {"start": v(41.23, -2.82) * mm, "end": v(43.2, -3) * mm});
            skLineSegment(sketch, "E21.25.3", {"start": v(41.13, -3.81) * mm, "end": v(41.04, -4.8) * mm});
            skLineSegment(sketch, "E21.25.4", {"start": v(41.13, -3.81) * mm, "end": v(41.23, -2.82) * mm});
            skLineSegment(sketch, "E21.25.5", {"start": v(43.2, -3) * mm, "end": v(43.45, -3.02) * mm});
            skArc(sketch, "E21.25.6", {"start": v(43.45, -3.02) * mm, "mid": v(43.4, -2.84) * mm, "end": v(43.22, -2.75) * mm});
            skArc(sketch, "E21.25.7", {"start": v(43, -5.24) * mm, "mid": v(43.18, -5.19) * mm, "end": v(43.27, -5.01) * mm});
            skLineSegment(sketch, "E21.25.8", {"start": v(43.02, -5) * mm, "end": v(43.27, -5.01) * mm});
            skLineSegment(sketch, "E21.25.9", {"start": v(43, -5.24) * mm, "end": v(43, -5.24) * mm});
            skLineSegment(sketch, "E21.25.10", {"start": v(43.23, -2.75) * mm, "end": v(43.22, -2.75) * mm});
            skArc(sketch, "E21.26.0", {"start": v(43.22, -2.75) * mm, "mid": v(43.31, 0) * mm, "end": v(43.22, 2.75) * mm});
            skLineSegment(sketch, "E21.26.1", {"start": v(41.23, 2.82) * mm, "end": v(43.2, 3) * mm});
            skLineSegment(sketch, "E21.26.2", {"start": v(41.04, 4.8) * mm, "end": v(43.02, 5) * mm});
            skLineSegment(sketch, "E21.26.3", {"start": v(41.13, 3.81) * mm, "end": v(41.23, 2.82) * mm});
            skLineSegment(sketch, "E21.26.4", {"start": v(41.13, 3.81) * mm, "end": v(41.04, 4.8) * mm});
            skLineSegment(sketch, "E21.26.5", {"start": v(43.02, 5) * mm, "end": v(43.27, 5.01) * mm});
            skArc(sketch, "E21.26.6", {"start": v(43.27, 5.01) * mm, "mid": v(43.18, 5.19) * mm, "end": v(43, 5.24) * mm});
            skArc(sketch, "E21.26.7", {"start": v(43.22, 2.75) * mm, "mid": v(43.4, 2.84) * mm, "end": v(43.45, 3.02) * mm});
            skLineSegment(sketch, "E21.26.8", {"start": v(43.2, 3) * mm, "end": v(43.45, 3.02) * mm});
            skLineSegment(sketch, "E21.26.9", {"start": v(43.22, 2.75) * mm, "end": v(43.22, 2.75) * mm});
            skLineSegment(sketch, "E21.26.10", {"start": v(43, 5.24) * mm, "end": v(43, 5.24) * mm});
            skArc(sketch, "E21.27.0", {"start": v(43, 5.24) * mm, "mid": v(42.57, 7.96) * mm, "end": v(41.98, 10.65) * mm});
            skLineSegment(sketch, "E21.27.1", {"start": v(40, 10.34) * mm, "end": v(41.92, 10.89) * mm});
            skLineSegment(sketch, "E21.27.2", {"start": v(39.46, 12.27) * mm, "end": v(41.37, 12.81) * mm});
            skLineSegment(sketch, "E21.27.3", {"start": v(39.73, 11.3) * mm, "end": v(40, 10.34) * mm});
            skLineSegment(sketch, "E21.27.4", {"start": v(39.73, 11.3) * mm, "end": v(39.46, 12.27) * mm});
            skLineSegment(sketch, "E21.27.5", {"start": v(41.37, 12.81) * mm, "end": v(41.61, 12.88) * mm});
            skArc(sketch, "E21.27.6", {"start": v(41.61, 12.88) * mm, "mid": v(41.5, 13.03) * mm, "end": v(41.3, 13.05) * mm});
            skArc(sketch, "E21.27.7", {"start": v(41.98, 10.65) * mm, "mid": v(42.14, 10.76) * mm, "end": v(42.16, 10.96) * mm});
            skLineSegment(sketch, "E21.27.8", {"start": v(41.92, 10.89) * mm, "end": v(42.16, 10.96) * mm});
            skLineSegment(sketch, "E21.27.9", {"start": v(41.98, 10.65) * mm, "end": v(41.98, 10.65) * mm});
            skLineSegment(sketch, "E21.27.10", {"start": v(41.3, 13.05) * mm, "end": v(41.3, 13.05) * mm});
            skArc(sketch, "E21.28.0", {"start": v(41.3, 13.05) * mm, "mid": v(40.39, 15.65) * mm, "end": v(39.31, 18.18) * mm});
            skLineSegment(sketch, "E21.28.1", {"start": v(37.42, 17.52) * mm, "end": v(39.2, 18.4) * mm});
            skLineSegment(sketch, "E21.28.2", {"start": v(36.53, 19.3) * mm, "end": v(38.31, 20.2) * mm});
            skLineSegment(sketch, "E21.28.3", {"start": v(36.98, 18.41) * mm, "end": v(37.42, 17.52) * mm});
            skLineSegment(sketch, "E21.28.4", {"start": v(36.98, 18.41) * mm, "end": v(36.53, 19.3) * mm});
            skLineSegment(sketch, "E21.28.5", {"start": v(38.31, 20.2) * mm, "end": v(38.54, 20.3) * mm});
            skArc(sketch, "E21.28.6", {"start": v(38.54, 20.3) * mm, "mid": v(38.39, 20.43) * mm, "end": v(38.2, 20.42) * mm});
            skArc(sketch, "E21.28.7", {"start": v(39.31, 18.18) * mm, "mid": v(39.44, 18.32) * mm, "end": v(39.43, 18.52) * mm});
            skLineSegment(sketch, "E21.28.8", {"start": v(39.2, 18.4) * mm, "end": v(39.43, 18.52) * mm});
            skLineSegment(sketch, "E21.28.9", {"start": v(39.31, 18.18) * mm, "end": v(39.31, 18.18) * mm});
            skLineSegment(sketch, "E21.28.10", {"start": v(38.2, 20.42) * mm, "end": v(38.2, 20.42) * mm});
            skArc(sketch, "E21.29.0", {"start": v(38.2, 20.42) * mm, "mid": v(36.82, 22.8) * mm, "end": v(35.3, 25.1) * mm});
            skLineSegment(sketch, "E21.29.1", {"start": v(33.57, 24.1) * mm, "end": v(35.16, 25.3) * mm});
            skLineSegment(sketch, "E21.29.2", {"start": v(32.36, 25.7) * mm, "end": v(33.95, 26.9) * mm});
            skLineSegment(sketch, "E21.29.3", {"start": v(32.97, 24.9) * mm, "end": v(33.57, 24.1) * mm});
            skLineSegment(sketch, "E21.29.4", {"start": v(32.97, 24.9) * mm, "end": v(32.36, 25.7) * mm});
            skLineSegment(sketch, "E21.29.5", {"start": v(33.95, 26.9) * mm, "end": v(34.15, 27.04) * mm});
            skArc(sketch, "E21.29.6", {"start": v(34.15, 27.04) * mm, "mid": v(33.98, 27.14) * mm, "end": v(33.8, 27.09) * mm});
            skArc(sketch, "E21.29.7", {"start": v(35.3, 25.1) * mm, "mid": v(35.4, 25.26) * mm, "end": v(35.36, 25.45) * mm});
            skLineSegment(sketch, "E21.29.8", {"start": v(35.16, 25.3) * mm, "end": v(35.36, 25.45) * mm});
            skLineSegment(sketch, "E21.29.9", {"start": v(35.3, 25.1) * mm, "end": v(35.3, 25.1) * mm});
            skLineSegment(sketch, "E21.29.10", {"start": v(33.8, 27.1) * mm, "end": v(33.8, 27.09) * mm});
            skArc(sketch, "E21.30.0", {"start": v(33.8, 27.09) * mm, "mid": v(32, 29.18) * mm, "end": v(30.09, 31.15) * mm});
            skLineSegment(sketch, "E21.30.1", {"start": v(28.57, 29.85) * mm, "end": v(29.9, 31.32) * mm});
            skLineSegment(sketch, "E21.30.2", {"start": v(27.1, 31.2) * mm, "end": v(28.43, 32.67) * mm});
            skLineSegment(sketch, "E21.30.3", {"start": v(27.83, 30.53) * mm, "end": v(28.57, 29.85) * mm});
            skLineSegment(sketch, "E21.30.4", {"start": v(27.83, 30.53) * mm, "end": v(27.1, 31.2) * mm});
            skLineSegment(sketch, "E21.30.5", {"start": v(28.43, 32.67) * mm, "end": v(28.6, 32.86) * mm});
            skArc(sketch, "E21.30.6", {"start": v(28.6, 32.86) * mm, "mid": v(28.42, 32.92) * mm, "end": v(28.24, 32.84) * mm});
            skArc(sketch, "E21.30.7", {"start": v(30.09, 31.15) * mm, "mid": v(30.16, 31.33) * mm, "end": v(30.08, 31.5) * mm});
            skLineSegment(sketch, "E21.30.8", {"start": v(29.9, 31.32) * mm, "end": v(30.08, 31.5) * mm});
            skLineSegment(sketch, "E21.30.9", {"start": v(30.09, 31.15) * mm, "end": v(30.09, 31.15) * mm});
            skLineSegment(sketch, "E21.30.10", {"start": v(28.25, 32.84) * mm, "end": v(28.24, 32.84) * mm});
            skArc(sketch, "E21.31.0", {"start": v(28.24, 32.84) * mm, "mid": v(26.1, 34.56) * mm, "end": v(23.85, 36.15) * mm});
            skLineSegment(sketch, "E21.31.1", {"start": v(22.6, 34.6) * mm, "end": v(23.64, 36.29) * mm});
            skLineSegment(sketch, "E21.31.2", {"start": v(20.9, 35.65) * mm, "end": v(21.94, 37.34) * mm});
            skLineSegment(sketch, "E21.31.3", {"start": v(21.75, 35.12) * mm, "end": v(22.6, 34.6) * mm});
            skLineSegment(sketch, "E21.31.4", {"start": v(21.75, 35.12) * mm, "end": v(20.9, 35.65) * mm});
            skLineSegment(sketch, "E21.31.5", {"start": v(21.94, 37.34) * mm, "end": v(22.08, 37.55) * mm});
            skArc(sketch, "E21.31.6", {"start": v(22.08, 37.55) * mm, "mid": v(21.88, 37.58) * mm, "end": v(21.73, 37.47) * mm});
            skArc(sketch, "E21.31.7", {"start": v(23.85, 36.15) * mm, "mid": v(23.89, 36.34) * mm, "end": v(23.78, 36.5) * mm});
            skLineSegment(sketch, "E21.31.8", {"start": v(23.64, 36.29) * mm, "end": v(23.78, 36.5) * mm});
            skLineSegment(sketch, "E21.31.9", {"start": v(23.85, 36.15) * mm, "end": v(23.85, 36.15) * mm});
            skLineSegment(sketch, "E21.31.10", {"start": v(21.73, 37.47) * mm, "end": v(21.73, 37.47) * mm});
            skArc(sketch, "E21.32.0", {"start": v(21.73, 37.47) * mm, "mid": v(19.3, 38.77) * mm, "end": v(16.8, 39.92) * mm});
            skLineSegment(sketch, "E21.32.1", {"start": v(15.86, 38.16) * mm, "end": v(16.57, 40.01) * mm});
            skLineSegment(sketch, "E21.32.2", {"start": v(14, 38.88) * mm, "end": v(14.7, 40.74) * mm});
            skLineSegment(sketch, "E21.32.3", {"start": v(14.92, 38.52) * mm, "end": v(15.86, 38.16) * mm});
            skLineSegment(sketch, "E21.32.4", {"start": v(14.92, 38.52) * mm, "end": v(14, 38.88) * mm});
            skLineSegment(sketch, "E21.32.5", {"start": v(14.7, 40.74) * mm, "end": v(14.8, 40.97) * mm});
            skArc(sketch, "E21.32.6", {"start": v(14.8, 40.97) * mm, "mid": v(14.6, 40.96) * mm, "end": v(14.47, 40.82) * mm});
            skArc(sketch, "E21.32.7", {"start": v(16.8, 39.92) * mm, "mid": v(16.8, 40.11) * mm, "end": v(16.66, 40.25) * mm});
            skLineSegment(sketch, "E21.32.8", {"start": v(16.57, 40.01) * mm, "end": v(16.66, 40.25) * mm});
            skLineSegment(sketch, "E21.32.9", {"start": v(16.8, 39.92) * mm, "end": v(16.8, 39.92) * mm});
            skLineSegment(sketch, "E21.32.10", {"start": v(14.48, 40.83) * mm, "end": v(14.47, 40.82) * mm});
            skArc(sketch, "E21.33.0", {"start": v(14.47, 40.82) * mm, "mid": v(11.85, 41.66) * mm, "end": v(9.18, 42.33) * mm});
            skLineSegment(sketch, "E21.33.1", {"start": v(8.57, 40.42) * mm, "end": v(8.94, 42.38) * mm});
            skLineSegment(sketch, "E21.33.2", {"start": v(6.6, 40.8) * mm, "end": v(6.97, 42.74) * mm});
            skLineSegment(sketch, "E21.33.3", {"start": v(7.6, 40.6) * mm, "end": v(8.57, 40.42) * mm});
            skLineSegment(sketch, "E21.33.4", {"start": v(7.6, 40.6) * mm, "end": v(6.6, 40.8) * mm});
            skLineSegment(sketch, "E21.33.5", {"start": v(6.97, 42.74) * mm, "end": v(7.02, 43) * mm});
            skArc(sketch, "E21.33.6", {"start": v(7.02, 43) * mm, "mid": v(6.83, 42.95) * mm, "end": v(6.73, 42.78) * mm});
            skArc(sketch, "E21.33.7", {"start": v(9.18, 42.33) * mm, "mid": v(9.15, 42.52) * mm, "end": v(8.98, 42.62) * mm});
            skLineSegment(sketch, "E21.33.8", {"start": v(8.94, 42.38) * mm, "end": v(8.98, 42.62) * mm});
            skLineSegment(sketch, "E21.33.9", {"start": v(9.18, 42.33) * mm, "end": v(9.18, 42.33) * mm});
            skLineSegment(sketch, "E21.33.10", {"start": v(6.73, 42.8) * mm, "end": v(6.73, 42.78) * mm});
            skCircle(sketch, "E22", {"center": v(0, 0) * mm, "radius": 44.25 * mm});
            skSolve(sketch);
        }
        {
            var Q0;
            Q0=makeQuery(id+"F7.imprint","IMPRINT",FACE,{"disambiguationData":[TD([[makeQuery(id+"F7.imprint","IMPRINT",EDGE,{"derivedFrom":sQuery(id+"F7.wireOp",EDGE,"E10")}),1.0]])]});
            extrude(context, id + "F8", {"entities" : qUnion([Q0]), "operationType" : NewBodyOperationType.ADD, "depth" : 10 * mm, "hasSecondDirection" : true, "secondDirectionOppositeDirection" : true, "secondDirectionDepth" : 10 * mm});
        }
        {
            var Q0;
            Q0=qCreatedBy(id+"F0.planeOp",FACE);
            var sketch = newSketch(context, id + "F9", { "sketchPlane" : qUnion([Q0])});
            skLineSegment(sketch, "E23", {"start": v(0, 0) * mm, "end": v(44.25, 0) * mm});
            skLineSegment(sketch, "E24", {"start": v(44.25, 0) * mm, "end": v(46.25, 0) * mm});
            skLineSegment(sketch, "E25", {"start": v(46.25, 0) * mm, "end": v(46.25, 5) * mm});
            skLineSegment(sketch, "E26", {"start": v(46.25, 0) * mm, "end": v(46.25, -5) * mm});
            skLineSegment(sketch, "E27", {"start": v(44.25, 0) * mm, "end": v(44.25, 10) * mm});
            skLineSegment(sketch, "E28", {"start": v(44.25, 0) * mm, "end": v(44.25, -10) * mm});
            skFitSpline(sketch, "E29", {"points": [v(44.25, -10) * mm, v(46.25, 0) * mm, v(44.25, 10) * mm], "startDerivative": vector(12, 30) * mm, "endDerivative": vector(-12, 30) * mm});
            skLineSegment(sketch, "E30", {"start": v(44.25, 10) * mm, "end": v(46.25, 10) * mm});
            skLineSegment(sketch, "E31", {"start": v(46.25, 10) * mm, "end": v(46.25, 5) * mm});
            skLineSegment(sketch, "E32", {"start": v(44.25, -10) * mm, "end": v(46.25, -10) * mm});
            skLineSegment(sketch, "E33", {"start": v(46.25, -10) * mm, "end": v(46.25, -5) * mm});
            skSolve(sketch);
        }
        {
            var Q0;
            Q0=qCreatedBy(makeId("Front.planeOp"),FACE);
            var sketch = newSketch(context, id + "F10", { "sketchPlane" : qUnion([Q0])});
            skLineSegment(sketch, "E34.0", {"start": v(44.25, 10) * mm, "end": v(46.25, 10) * mm});
            skLineSegment(sketch, "E34.1", {"start": v(46.25, 10) * mm, "end": v(46.25, 5) * mm});
            skFitSpline(sketch, "E34.2", {"points": [v(44.25, -10) * mm, v(46.25, -5) * mm, v(46.25, 0) * mm, v(46.25, 5) * mm, v(44.25, 10) * mm]});
            skLineSegment(sketch, "E34.3", {"start": v(46.25, 0) * mm, "end": v(46.25, 5) * mm});
            skLineSegment(sketch, "E34.4", {"start": v(46.25, -10) * mm, "end": v(46.25, -5) * mm});
            skLineSegment(sketch, "E34.5", {"start": v(46.25, 0) * mm, "end": v(46.25, -5) * mm});
            skLineSegment(sketch, "E34.6", {"start": v(44.25, -10) * mm, "end": v(46.25, -10) * mm});
            skFitSpline(sketch, "E35.2", {"points": [v(44.25, -10) * mm, v(46.25, -5) * mm, v(46.25, 0) * mm, v(46.25, 5) * mm, v(44.25, 10) * mm]});
            skSolve(sketch);
        }
        {
            var Q0;
            {var subQ2=sQuery(id+"F10.wireOp",EDGE,"E34.0");Q0=makeQuery(id+"F10.imprint","IMPRINT",FACE,{"disambiguationData":[TD([[makeQuery(id+"F10.imprint","IMPRINT",EDGE,{"derivedFrom":subQ2}),-1.0]])]});}
            var Q1;
            Q1=makeQuery(id+"F10.imprint","IMPRINT",FACE,{"disambiguationData":[TD([[makeQuery(id+"F10.imprint","IMPRINT",EDGE,{"derivedFrom":sQuery(id+"F10.wireOp",EDGE,"E34.4")}),1.0]])]});
            var Q2;
            Q2=sQuery(id+"F3.wireOp",EDGE,"E8");
            revolve(context, id + "F11", {"operationType" : NewBodyOperationType.REMOVE, "entities" : qUnion([Q0, Q1]), "axis" : qUnion([Q2]), "revolveType" : RevolveType.FULL});
        }
        {
            var Q0;
            Q0=qCreatedBy(makeId("Right.planeOp"),FACE);
            var sketch = newSketch(context, id + "F12", { "sketchPlane" : qUnion([Q0])});
            skLineSegment(sketch, "E36", {"start": v(41.81, -3.75) * mm, "end": v(41.81, 3.75) * mm});
            skLineSegment(sketch, "E37", {"start": v(41.81, -3.75) * mm, "end": v(41.31, -3.75) * mm});
            skLineSegment(sketch, "E38", {"start": v(38.3, -0.75) * mm, "end": v(38.3, 0.75) * mm});
            skLineSegment(sketch, "E39", {"start": v(41.31, 3.75) * mm, "end": v(38.3, 0.75) * mm});
            skLineSegment(sketch, "E40", {"start": v(41.31, -3.75) * mm, "end": v(38.3, -0.75) * mm});
            skLineSegment(sketch, "E41", {"start": v(41.31, 3.75) * mm, "end": v(41.81, 3.75) * mm});
            skSolve(sketch);
        }
        {
            var Q0;
            Q0 = qSketchRegion(id + "F12", true);
            extrude(context, id + "F13", {"entities" : qUnion([Q0]), "depth" : 1 * mm, "hasSecondDirection" : true, "secondDirectionOppositeDirection" : true, "secondDirectionDepth" : 1 * mm});
        }
        {
            var Q0;
            Q0=makeQuery(id+"F13.opExtrude","SWEPT_BODY",BODY,{"disambiguationData":[OSD([sQuery(id+"F12.wireOp",EDGE,"E36"),sQuery(id+"F12.wireOp",EDGE,"E37"),sQuery(id+"F12.wireOp",EDGE,"E38"),sQuery(id+"F12.wireOp",EDGE,"E39"),sQuery(id+"F12.wireOp",EDGE,"E40"),sQuery(id+"F12.wireOp",EDGE,"E41")])]});
            var Q1;
            Q1=sQuery(id+"F3.wireOp",EDGE,"E8");
            circularPattern(context, id + "F14", {"operationType" : NewBodyOperationType.ADD, "entities" : qUnion([Q0]), "axis" : qUnion([Q1]), "angle" : 360 * degree, "instanceCount" : 34, "equalSpace" : true});
        }
    });
